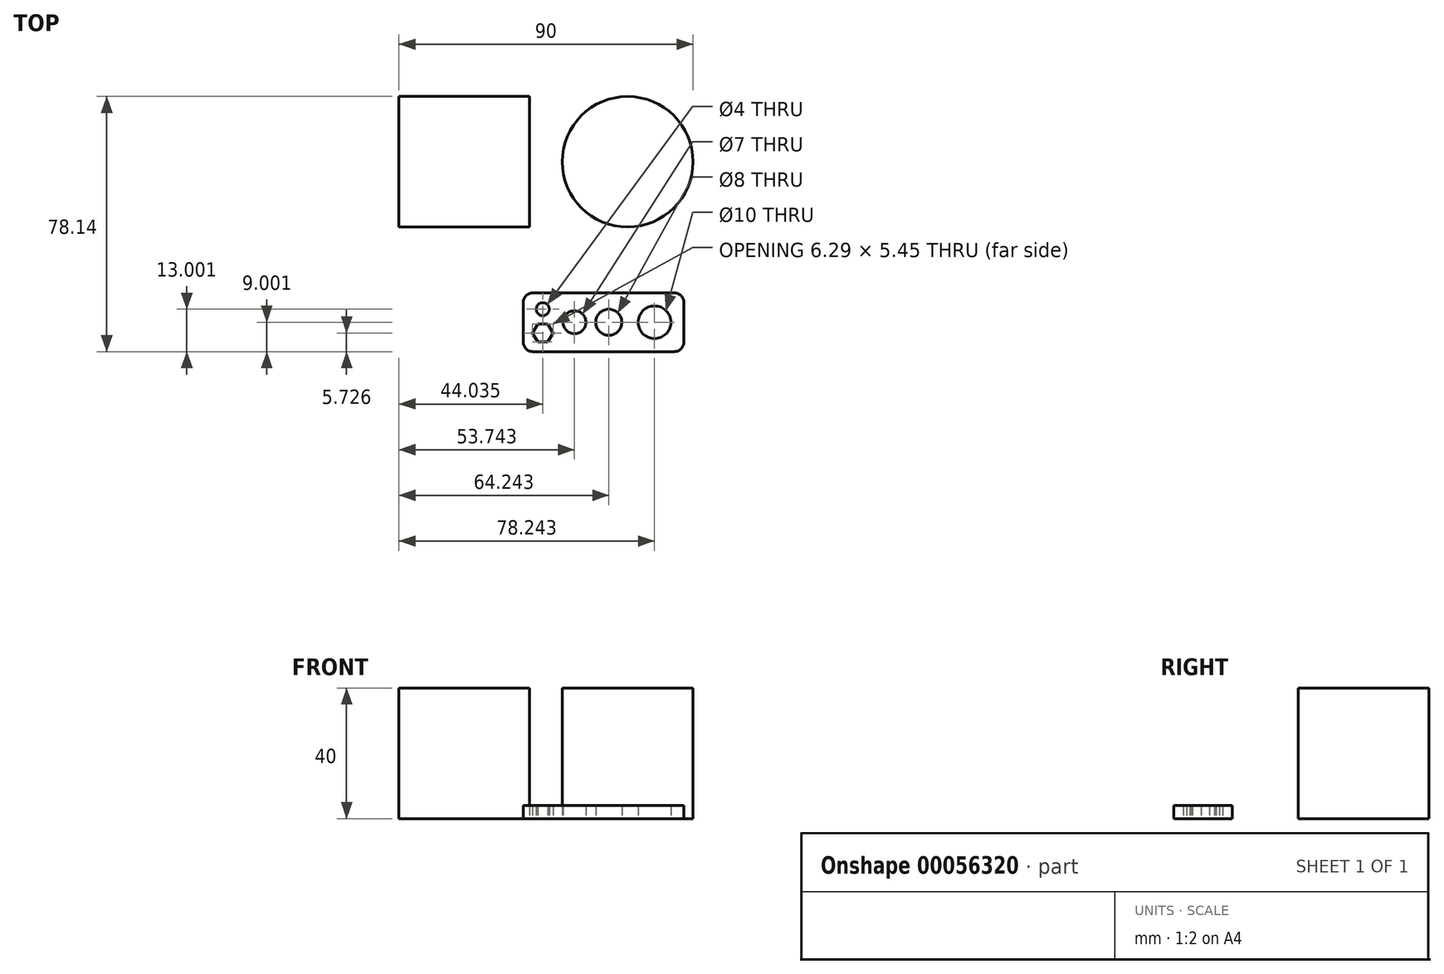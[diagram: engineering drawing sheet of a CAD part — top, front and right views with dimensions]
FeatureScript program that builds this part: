
annotation { "Feature Type Name" : "Feature", "Feature Type Description" : "" }
export const myFeature = defineFeature(function(context is Context, id is Id, definition is map)
    precondition{}
    {
        {
            var Q0;
            Q0=qCreatedBy(makeId("Top.planeOp"),FACE);
            var sketch = newSketch(context, id + "F0", { "sketchPlane" : qUnion([Q0])});
            skLineSegment(sketch, "E0.bottom", {"start": v(20, 20) * mm, "end": v(-20, 20) * mm});
            skLineSegment(sketch, "E0.top", {"start": v(20, -20) * mm, "end": v(-20, -20) * mm});
            skLineSegment(sketch, "E0.left", {"start": v(20, 20) * mm, "end": v(20, -20) * mm});
            skLineSegment(sketch, "E0.right", {"start": v(-20, 20) * mm, "end": v(-20, -20) * mm});
            skPoint(sketch, "E0.middle", {"position": v(0, 0) * mm});
            skSolve(sketch);
        }
        {
            var Q0;
            Q0 = qSketchRegion(id + "F0", true);
            extrude(context, id + "F1", {"entities" : qUnion([Q0]), "depth" : 40 * mm, "offsetDistance" : 25 * mm});
        }
        {
            var Q0;
            Q0=qCreatedBy(makeId("Top.planeOp"),FACE);
            var sketch = newSketch(context, id + "F2", { "sketchPlane" : qUnion([Q0])});
            skCircle(sketch, "E1", {"center": v(50, 0) * mm, "radius": 20 * mm});
            skSolve(sketch);
        }
        {
            var Q0;
            Q0 = qSketchRegion(id + "F2", true);
            var Q1;
            Q1=makeQuery(id+"F1.opExtrude","CAP_FACE",FACE,{"disambiguationData":[OSD([sQuery(id+"F0.wireOp",EDGE,"E0.bottom"),sQuery(id+"F0.wireOp",EDGE,"E0.top"),sQuery(id+"F0.wireOp",EDGE,"E0.left"),sQuery(id+"F0.wireOp",EDGE,"E0.right")])],"isStart":false});
            extrude(context, id + "F3", {"entities" : qUnion([Q0]), "endBound" : BoundingType.UP_TO_SURFACE, "depth" : 25 * mm, "endBoundEntityFace" : qUnion([Q1]), "offsetDistance" : 25 * mm});
        }
        {
            var Q0;
            Q0=qCreatedBy(makeId("Top.planeOp"),FACE);
            var sketch = newSketch(context, id + "F4", { "sketchPlane" : qUnion([Q0])});
            skCircle(sketch, "E2", {"center": v(24.03, -45.14) * mm, "radius": 2 * mm});
            skCircle(sketch, "E3", {"center": v(33.74, -49.14) * mm, "radius": 3.5 * mm});
            skCircle(sketch, "E4", {"center": v(44.24, -49.14) * mm, "radius": 4 * mm});
            skCircle(sketch, "E5", {"center": v(58.24, -49.14) * mm, "radius": 5 * mm});
            skLineSegment(sketch, "E6.bottom", {"start": v(21.03, -40.14) * mm, "end": v(64.24, -40.14) * mm});
            skLineSegment(sketch, "E6.top", {"start": v(21.03, -58.14) * mm, "end": v(64.24, -58.14) * mm});
            skLineSegment(sketch, "E6.left", {"start": v(18.03, -43.14) * mm, "end": v(18.03, -55.14) * mm});
            skLineSegment(sketch, "E6.right", {"start": v(67.24, -43.14) * mm, "end": v(67.24, -55.14) * mm});
            skPoint(sketch, "E7.visualSharp", {"position": v(18.03, -40.14) * mm});
            skArc(sketch, "E7.filletArc", {"start": v(21.03, -40.14) * mm, "mid": v(18.91, -41.02) * mm, "end": v(18.03, -43.14) * mm});
            skPoint(sketch, "E8.visualSharp", {"position": v(67.24, -40.14) * mm});
            skArc(sketch, "E8.filletArc", {"start": v(67.24, -43.14) * mm, "mid": v(66.36, -41.02) * mm, "end": v(64.24, -40.14) * mm});
            skPoint(sketch, "E9.visualSharp", {"position": v(67.24, -58.14) * mm});
            skArc(sketch, "E9.filletArc", {"start": v(64.24, -58.14) * mm, "mid": v(66.36, -57.26) * mm, "end": v(67.24, -55.14) * mm});
            skPoint(sketch, "E10.visualSharp", {"position": v(18.03, -58.14) * mm});
            skArc(sketch, "E10.filletArc", {"start": v(18.03, -55.14) * mm, "mid": v(18.91, -57.26) * mm, "end": v(21.03, -58.14) * mm});
            skCircle(sketch, "E11.cCircle", {"center": v(24.03, -52.41) * mm, "radius": 2.72 * mm, "construction": true});
            skLineSegment(sketch, "E11.0", {"start": v(27.18, -52.41) * mm, "end": v(25.6, -55.14) * mm});
            skLineSegment(sketch, "E11.1", {"start": v(25.6, -55.14) * mm, "end": v(22.46, -55.14) * mm});
            skLineSegment(sketch, "E11.2", {"start": v(22.46, -55.14) * mm, "end": v(20.89, -52.41) * mm});
            skLineSegment(sketch, "E11.3", {"start": v(20.89, -52.41) * mm, "end": v(22.46, -49.69) * mm});
            skLineSegment(sketch, "E11.4", {"start": v(22.46, -49.69) * mm, "end": v(25.6, -49.69) * mm});
            skLineSegment(sketch, "E11.5", {"start": v(25.6, -49.69) * mm, "end": v(27.18, -52.41) * mm});
            skPoint(sketch, "E11.0.midPoint", {"position": v(26.4, -53.78) * mm});
            skSolve(sketch);
        }
        {
            var Q0;
            Q0 = qSketchRegion(id + "F4", true);
            extrude(context, id + "F5", {"entities" : qUnion([Q0]), "depth" : 4 * mm, "offsetDistance" : 25 * mm});
        }
    });
